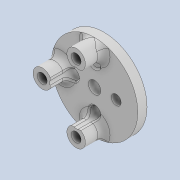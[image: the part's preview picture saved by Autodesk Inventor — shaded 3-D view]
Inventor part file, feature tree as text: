
AUTODESK INVENTOR PART (.ipt)
format: ipt  version: 2020 (Build 240168000, 168)  size: 315,392 bytes
history: native  units: mm
features: reference x6, other x4, extrude x3, sketch x3, plane x1, fillet x1, chamfer x1, projected_geometry x1
ambient origin geometry x8: Origin, YZ Plane, XZ Plane, XY Plane, X Axis, Y Axis, Z Axis, Center Point
bodies: Solid1 (feature_tree)
feature tree (20):
  extrude  "Extrusion1"  Depth=3.0mm TaperAngle=0.0deg
  sketch  "Sketch2"  dims[d3=6.0mm d4=6.0mm]
  plane  "Work Plane1"
  extrude  "Extrusion2"  Depth=6.0mm
  extrude  "Extrusion3"  Depth=3.0mm TaperAngle=0.0deg
  fillet  "Fillet1"  Radius=4.0mm
  chamfer  "Chamfer1"  Distance=3.0mm
  sketch  "Sketch1"  dims[d0=28.0mm d1=3.0mm d2=0.0mm]
  reference  "Reference1"
  reference  "Reference2"
  reference  "Reference3"
  reference  "Reference4"
  reference  "Reference5"
  reference  "Reference6"
  projected_geometry  "Projected Loop1"
  sketch  "Sketch3"  dims[d5=6.0mm d6=3.0mm d7=0.0mm d8=4.0mm d9=3.0mm d10=0.0mm d11=2.0mm d12=0.5mm d13=2.0mm d14=45.0deg]
  parser-record x1  (decoder bookkeeping rows leaked as tree rows — omitted from the tree; the rows remain in map.json)
  other  "driver_unit_1.iam"
  other  "driver_wheel_1:1"
  other  "tendon_wh_3:1"
note: 1 file-system path scrubbed to <path> (originals preserved in map.json)
